annotation { "Feature Type Name" : "Feature", "Feature Type Description" : "" }
export const myFeature = defineFeature(function(context is Context, id is Id, definition is map)
    precondition{}
    {
        {
            var Q0;
            Q0=qCreatedBy(makeId("Front.planeOp"),FACE);
            var sketch = newSketch(context, id + "F0", { "sketchPlane" : qUnion([Q0])});
            skLineSegment(sketch, "E0.bottom", {"start": v(145.5, 75.5) * mm, "end": v(-145.5, 75.5) * mm});
            skLineSegment(sketch, "E0.top", {"start": v(145.5, -75.5) * mm, "end": v(-145.5, -75.5) * mm});
            skLineSegment(sketch, "E0.left", {"start": v(155.5, 65.5) * mm, "end": v(155.5, -65.5) * mm});
            skLineSegment(sketch, "E0.right", {"start": v(-155.5, 65.5) * mm, "end": v(-155.5, -65.5) * mm});
            skPoint(sketch, "E0.middle", {"position": v(0, 0) * mm});
            skLineSegment(sketch, "E1.bottom", {"start": v(135.5, 60.5) * mm, "end": v(-135.5, 60.5) * mm});
            skLineSegment(sketch, "E1.left", {"start": v(140.5, 55.5) * mm, "end": v(140.5, -30.5) * mm});
            skLineSegment(sketch, "E1.right", {"start": v(-140.5, 55.5) * mm, "end": v(-140.5, -35.5) * mm});
            skLineSegment(sketch, "E2", {"start": v(-135.5, -40.5) * mm, "end": v(130.5, -40.5) * mm});
            skPoint(sketch, "E3.orphan", {"position": v(140.5, -60.5) * mm});
            skPoint(sketch, "E4.orphan", {"position": v(-140.5, -60.5) * mm});
            skPoint(sketch, "E5.visualSharp", {"position": v(-155.5, 75.5) * mm});
            skArc(sketch, "E5.filletArc", {"start": v(-145.5, 75.5) * mm, "mid": v(-152.57, 72.57) * mm, "end": v(-155.5, 65.5) * mm});
            skPoint(sketch, "E6.visualSharp", {"position": v(-155.5, -75.5) * mm});
            skArc(sketch, "E6.filletArc", {"start": v(-155.5, -65.5) * mm, "mid": v(-152.57, -72.57) * mm, "end": v(-145.5, -75.5) * mm});
            skPoint(sketch, "E7.visualSharp", {"position": v(155.5, 75.5) * mm});
            skArc(sketch, "E7.filletArc", {"start": v(155.5, 65.5) * mm, "mid": v(152.57, 72.57) * mm, "end": v(145.5, 75.5) * mm});
            skPoint(sketch, "E8.visualSharp", {"position": v(155.5, -75.5) * mm});
            skArc(sketch, "E8.filletArc", {"start": v(145.5, -75.5) * mm, "mid": v(152.57, -72.57) * mm, "end": v(155.5, -65.5) * mm});
            skPoint(sketch, "E9.visualSharp", {"position": v(-140.5, 60.5) * mm});
            skArc(sketch, "E9.filletArc", {"start": v(-135.5, 60.5) * mm, "mid": v(-139.04, 59.04) * mm, "end": v(-140.5, 55.5) * mm});
            skPoint(sketch, "E10.visualSharp", {"position": v(-140.5, -40.5) * mm});
            skArc(sketch, "E10.filletArc", {"start": v(-140.5, -35.5) * mm, "mid": v(-139.04, -39.04) * mm, "end": v(-135.5, -40.5) * mm});
            skPoint(sketch, "E11.visualSharp", {"position": v(140.5, -40.5) * mm});
            skArc(sketch, "E11.filletArc", {"start": v(130.5, -40.5) * mm, "mid": v(137.57, -37.57) * mm, "end": v(140.5, -30.5) * mm});
            skPoint(sketch, "E12.visualSharp", {"position": v(140.5, 60.5) * mm});
            skArc(sketch, "E12.filletArc", {"start": v(140.5, 55.5) * mm, "mid": v(139.04, 59.04) * mm, "end": v(135.5, 60.5) * mm});
            skSolve(sketch);
        }
        {
            var Q0;
            Q0=qSketchRegion(id+"F0",true);
            extrude(context, id + "F1", {"entities" : qUnion([Q0]), "depth" : 1.6 * mm, "offsetDistance" : 25 * mm});
        }
        {
            var Q0;
            Q0=makeQuery(id+"F1.opExtrude","CAP_FACE",FACE,{"disambiguationData":[OSD([sQuery(id+"F0.wireOp",EDGE,"E0.bottom"),sQuery(id+"F0.wireOp",EDGE,"E0.top"),sQuery(id+"F0.wireOp",EDGE,"E0.left"),sQuery(id+"F0.wireOp",EDGE,"E0.right"),sQuery(id+"F0.wireOp",EDGE,"E1.bottom"),sQuery(id+"F0.wireOp",EDGE,"E1.left"),sQuery(id+"F0.wireOp",EDGE,"E1.right"),sQuery(id+"F0.wireOp",EDGE,"E2"),sQuery(id+"F0.wireOp",EDGE,"E5.filletArc"),sQuery(id+"F0.wireOp",EDGE,"E6.filletArc"),sQuery(id+"F0.wireOp",EDGE,"E7.filletArc"),sQuery(id+"F0.wireOp",EDGE,"E8.filletArc"),sQuery(id+"F0.wireOp",EDGE,"E9.filletArc"),sQuery(id+"F0.wireOp",EDGE,"E10.filletArc"),sQuery(id+"F0.wireOp",EDGE,"E11.filletArc"),sQuery(id+"F0.wireOp",EDGE,"E12.filletArc")])],"isStart":false});
            var sketch = newSketch(context, id + "F2", { "sketchPlane" : qUnion([Q0])});
            skLineSegment(sketch, "E13.bottom", {"start": v(-101, 60.5) * mm, "end": v(-76, 60.5) * mm});
            skLineSegment(sketch, "E13.top", {"start": v(-101, 44.5) * mm, "end": v(-76, 44.5) * mm});
            skLineSegment(sketch, "E13.left", {"start": v(-101, 60.5) * mm, "end": v(-101, 44.5) * mm});
            skLineSegment(sketch, "E13.right", {"start": v(-76, 60.5) * mm, "end": v(-76, 44.5) * mm});
            skLineSegment(sketch, "E14.bottom", {"start": v(76, 60.5) * mm, "end": v(101, 60.5) * mm});
            skLineSegment(sketch, "E14.top", {"start": v(76, 44.5) * mm, "end": v(101, 44.5) * mm});
            skLineSegment(sketch, "E14.left", {"start": v(76, 60.5) * mm, "end": v(76, 44.5) * mm});
            skLineSegment(sketch, "E14.right", {"start": v(101, 60.5) * mm, "end": v(101, 44.5) * mm});
            skLineSegment(sketch, "E15", {"start": v(-88.5, 44.5) * mm, "end": v(-88.5, 60.5) * mm, "construction": true});
            skLineSegment(sketch, "E16", {"start": v(-101, 44.5) * mm, "end": v(-140.5, 44.5) * mm, "construction": true});
            skLineSegment(sketch, "E17", {"start": v(101, 44.5) * mm, "end": v(140.5, 44.5) * mm, "construction": true});
            skSolve(sketch);
        }
        {
            var Q0;
            Q0=qSketchRegion(id+"F2",true);
            var Q1;
            Q1=makeQuery(id+"F1.opExtrude","CAP_FACE",FACE,{"disambiguationData":[OSD([sQuery(id+"F0.wireOp",EDGE,"E0.bottom"),sQuery(id+"F0.wireOp",EDGE,"E0.top"),sQuery(id+"F0.wireOp",EDGE,"E0.left"),sQuery(id+"F0.wireOp",EDGE,"E0.right"),sQuery(id+"F0.wireOp",EDGE,"E1.bottom"),sQuery(id+"F0.wireOp",EDGE,"E1.left"),sQuery(id+"F0.wireOp",EDGE,"E1.right"),sQuery(id+"F0.wireOp",EDGE,"E2"),sQuery(id+"F0.wireOp",EDGE,"E5.filletArc"),sQuery(id+"F0.wireOp",EDGE,"E6.filletArc"),sQuery(id+"F0.wireOp",EDGE,"E7.filletArc"),sQuery(id+"F0.wireOp",EDGE,"E8.filletArc"),sQuery(id+"F0.wireOp",EDGE,"E9.filletArc"),sQuery(id+"F0.wireOp",EDGE,"E10.filletArc"),sQuery(id+"F0.wireOp",EDGE,"E11.filletArc"),sQuery(id+"F0.wireOp",EDGE,"E12.filletArc")])],"isStart":true});
            extrude(context, id + "F3", {"entities" : qUnion([Q0]), "operationType" : NewBodyOperationType.ADD, "endBound" : BoundingType.UP_TO_SURFACE, "oppositeDirection" : true, "endBoundEntityFace" : qUnion([Q1]), "depth" : 25 * mm});
        }
        {
            var Q0;
            Q0=makeQuery(id+"F3.boolean.opBoolean","MERGE",FACE,{"derivedFrom":[makeQuery(id+"F1.opExtrude","CAP_FACE",FACE,{"disambiguationData":[OSD([sQuery(id+"F0.wireOp",EDGE,"E0.bottom"),sQuery(id+"F0.wireOp",EDGE,"E0.top"),sQuery(id+"F0.wireOp",EDGE,"E0.left"),sQuery(id+"F0.wireOp",EDGE,"E0.right"),sQuery(id+"F0.wireOp",EDGE,"E1.bottom"),sQuery(id+"F0.wireOp",EDGE,"E1.left"),sQuery(id+"F0.wireOp",EDGE,"E1.right"),sQuery(id+"F0.wireOp",EDGE,"E2"),sQuery(id+"F0.wireOp",EDGE,"E5.filletArc"),sQuery(id+"F0.wireOp",EDGE,"E6.filletArc"),sQuery(id+"F0.wireOp",EDGE,"E7.filletArc"),sQuery(id+"F0.wireOp",EDGE,"E8.filletArc"),sQuery(id+"F0.wireOp",EDGE,"E9.filletArc"),sQuery(id+"F0.wireOp",EDGE,"E10.filletArc"),sQuery(id+"F0.wireOp",EDGE,"E11.filletArc"),sQuery(id+"F0.wireOp",EDGE,"E12.filletArc")])],"isStart":false}),makeQuery(id+"F3.opExtrude","CAP_FACE",FACE,{"disambiguationData":[OSD([sQuery(id+"F2.wireOp",EDGE,"E13.bottom"),sQuery(id+"F2.wireOp",EDGE,"E13.top"),sQuery(id+"F2.wireOp",EDGE,"E13.left"),sQuery(id+"F2.wireOp",EDGE,"E13.right")])],"isStart":true}),makeQuery(id+"F3.opExtrude","CAP_FACE",FACE,{"disambiguationData":[OSD([sQuery(id+"F2.wireOp",EDGE,"E14.bottom"),sQuery(id+"F2.wireOp",EDGE,"E14.top"),sQuery(id+"F2.wireOp",EDGE,"E14.left"),sQuery(id+"F2.wireOp",EDGE,"E14.right")])],"isStart":true})]});
            var sketch = newSketch(context, id + "F4", { "sketchPlane" : qUnion([Q0])});
            skLineSegment(sketch, "E18", {"start": v(101, 60.5) * mm, "end": v(101, 64.5) * mm});
            skLineSegment(sketch, "E19", {"start": v(101, 64.5) * mm, "end": v(140.5, 64.5) * mm});
            skLineSegment(sketch, "E20", {"start": v(140.5, 55.5) * mm, "end": v(101, 55.5) * mm});
            skLineSegment(sketch, "E21", {"start": v(140.5, 55.5) * mm, "end": v(140.5, 64.5) * mm});
            skLineSegment(sketch, "E22", {"start": v(101, 60.5) * mm, "end": v(101, 55.5) * mm});
            skSolve(sketch);
        }
        {
            var Q0;
            Q0=qSketchRegion(id+"F4",true);
            extrude(context, id + "F5", {"entities" : qUnion([Q0]), "operationType" : NewBodyOperationType.REMOVE, "oppositeDirection" : true, "depth" : 25 * mm});
        }
        {
            var Q0;
            Q0=makeQuery(id+"F3.opExtrude","SWEPT_EDGE",EDGE,{"disambiguationData":[OSD([sQuery(id+"F2.wireOp",EDGE,"E13.top"),sQuery(id+"F2.wireOp",EDGE,"E13.left")])]});
            var Q1;
            Q1=makeQuery(id+"F3.opExtrude","SWEPT_EDGE",EDGE,{"disambiguationData":[OSD([sQuery(id+"F0.wireOp",EDGE,"E1.bottom"),sQuery(id+"F2.wireOp",EDGE,"E13.bottom"),sQuery(id+"F2.wireOp",EDGE,"E13.left")])]});
            var Q2;
            Q2=makeQuery(id+"F3.opExtrude","SWEPT_EDGE",EDGE,{"disambiguationData":[OSD([sQuery(id+"F2.wireOp",EDGE,"E13.top"),sQuery(id+"F2.wireOp",EDGE,"E13.right")])]});
            var Q3;
            Q3=makeQuery(id+"F3.opExtrude","SWEPT_EDGE",EDGE,{"disambiguationData":[OSD([sQuery(id+"F0.wireOp",EDGE,"E1.bottom"),sQuery(id+"F2.wireOp",EDGE,"E13.bottom"),sQuery(id+"F2.wireOp",EDGE,"E13.right")])]});
            var Q4;
            Q4=makeQuery(id+"F3.opExtrude","SWEPT_EDGE",EDGE,{"disambiguationData":[OSD([sQuery(id+"F2.wireOp",EDGE,"E14.top"),sQuery(id+"F2.wireOp",EDGE,"E14.right")])]});
            var Q5;
            Q5=makeQuery(id+"F3.opExtrude","SWEPT_EDGE",EDGE,{"disambiguationData":[OSD([sQuery(id+"F0.wireOp",EDGE,"E1.bottom"),sQuery(id+"F2.wireOp",EDGE,"E14.bottom"),sQuery(id+"F2.wireOp",EDGE,"E14.right")])]});
            var Q6;
            Q6=makeQuery(id+"F3.opExtrude","SWEPT_EDGE",EDGE,{"disambiguationData":[OSD([sQuery(id+"F2.wireOp",EDGE,"E14.top"),sQuery(id+"F2.wireOp",EDGE,"E14.left")])]});
            var Q7;
            Q7=makeQuery(id+"F3.opExtrude","SWEPT_EDGE",EDGE,{"disambiguationData":[OSD([sQuery(id+"F0.wireOp",EDGE,"E1.bottom"),sQuery(id+"F2.wireOp",EDGE,"E14.bottom"),sQuery(id+"F2.wireOp",EDGE,"E14.left")])]});
            var Q8;
            Q8=makeQuery(id+"F5.boolean.opBoolean","COPY",EDGE,{"derivedFrom":makeQuery(id+"F5.opExtrude","SWEPT_EDGE",EDGE,{"disambiguationData":[OSD([sQuery(id+"F4.wireOp",EDGE,"E19"),sQuery(id+"F4.wireOp",EDGE,"E21")])]})});
            fillet(context, id + "F6", {"entities" : qUnion([Q0, Q1, Q2, Q3, Q4, Q5, Q6, Q7, Q8]), "radius" : 5 * mm, "tangentPropagation" : true, "allowEdgeOverflow" : false});
        }
        {
            var Q0;
            Q0=makeQuery(id+"F5.boolean.opBoolean","COPY",EDGE,{"derivedFrom":makeQuery(id+"F5.opExtrude","SWEPT_EDGE",EDGE,{"disambiguationData":[OSD([sQuery(id+"F4.wireOp",EDGE,"7OP9Tv27-VSEW-8zX2-RoHM-HqM2cPaEEPGh"),sQuery(id+"F4.wireOp",EDGE,"E18")])]})});
            var Q1;
            Q1=makeQuery(id+"F5.boolean.opBoolean","COPY",EDGE,{"derivedFrom":makeQuery(id+"F5.opExtrude","SWEPT_EDGE",EDGE,{"disambiguationData":[OSD([sQuery(id+"F4.wireOp",EDGE,"aboeoGEW-dTeu-87r4-9ffM-jYBHCW7SDUxB"),sQuery(id+"F4.wireOp",EDGE,"7OP9Tv27-VSEW-8zX2-RoHM-HqM2cPaEEPGh")])]})});
            fillet(context, id + "F7", {"entities" : qUnion([Q0, Q1]), "radius" : 5 * mm, "tangentPropagation" : true, "allowEdgeOverflow" : false});
        }
        {
            var Q0;
            Q0=makeQuery(id+"F3.boolean.opBoolean","MERGE",FACE,{"derivedFrom":[makeQuery(id+"F1.opExtrude","CAP_FACE",FACE,{"disambiguationData":[OSD([sQuery(id+"F0.wireOp",EDGE,"E0.bottom"),sQuery(id+"F0.wireOp",EDGE,"E0.top"),sQuery(id+"F0.wireOp",EDGE,"E0.left"),sQuery(id+"F0.wireOp",EDGE,"E0.right"),sQuery(id+"F0.wireOp",EDGE,"E1.bottom"),sQuery(id+"F0.wireOp",EDGE,"E1.left"),sQuery(id+"F0.wireOp",EDGE,"E1.right"),sQuery(id+"F0.wireOp",EDGE,"E2"),sQuery(id+"F0.wireOp",EDGE,"E5.filletArc"),sQuery(id+"F0.wireOp",EDGE,"E6.filletArc"),sQuery(id+"F0.wireOp",EDGE,"E7.filletArc"),sQuery(id+"F0.wireOp",EDGE,"E8.filletArc"),sQuery(id+"F0.wireOp",EDGE,"E9.filletArc"),sQuery(id+"F0.wireOp",EDGE,"E10.filletArc"),sQuery(id+"F0.wireOp",EDGE,"E11.filletArc"),sQuery(id+"F0.wireOp",EDGE,"E12.filletArc")])],"isStart":false}),makeQuery(id+"F3.opExtrude","CAP_FACE",FACE,{"disambiguationData":[OSD([sQuery(id+"F2.wireOp",EDGE,"E13.bottom"),sQuery(id+"F2.wireOp",EDGE,"E13.top"),sQuery(id+"F2.wireOp",EDGE,"E13.left"),sQuery(id+"F2.wireOp",EDGE,"E13.right")])],"isStart":true}),makeQuery(id+"F3.opExtrude","CAP_FACE",FACE,{"disambiguationData":[OSD([sQuery(id+"F2.wireOp",EDGE,"E14.bottom"),sQuery(id+"F2.wireOp",EDGE,"E14.top"),sQuery(id+"F2.wireOp",EDGE,"E14.left"),sQuery(id+"F2.wireOp",EDGE,"E14.right")])],"isStart":true})]});
            var sketch = newSketch(context, id + "F8", { "sketchPlane" : qUnion([Q0])});
            skCircle(sketch, "E23", {"center": v(-88.5, 56.5) * mm, "radius": 5.5 * mm});
            skCircle(sketch, "E24", {"center": v(88.5, 56.5) * mm, "radius": 5.5 * mm});
            skLineSegment(sketch, "E25", {"start": v(-88.5, 44.5) * mm, "end": v(-88.5, 89.98) * mm, "construction": true});
            skLineSegment(sketch, "E26", {"start": v(88.5, 44.5) * mm, "end": v(88.5, 67.92) * mm, "construction": true});
            skSolve(sketch);
        }
        {
            var Q0;
            Q0=qSketchRegion(id+"F8",true);
            extrude(context, id + "F9", {"entities" : qUnion([Q0]), "operationType" : NewBodyOperationType.REMOVE, "oppositeDirection" : true, "depth" : 25 * mm});
        }
        {
            var Q0;
            Q0=makeQuery(id+"F3.boolean.opBoolean","MERGE",FACE,{"derivedFrom":[makeQuery(id+"F1.opExtrude","CAP_FACE",FACE,{"disambiguationData":[OSD([sQuery(id+"F0.wireOp",EDGE,"E0.bottom"),sQuery(id+"F0.wireOp",EDGE,"E0.top"),sQuery(id+"F0.wireOp",EDGE,"E0.left"),sQuery(id+"F0.wireOp",EDGE,"E0.right"),sQuery(id+"F0.wireOp",EDGE,"E1.bottom"),sQuery(id+"F0.wireOp",EDGE,"E1.left"),sQuery(id+"F0.wireOp",EDGE,"E1.right"),sQuery(id+"F0.wireOp",EDGE,"E2"),sQuery(id+"F0.wireOp",EDGE,"E5.filletArc"),sQuery(id+"F0.wireOp",EDGE,"E6.filletArc"),sQuery(id+"F0.wireOp",EDGE,"E7.filletArc"),sQuery(id+"F0.wireOp",EDGE,"E8.filletArc"),sQuery(id+"F0.wireOp",EDGE,"E9.filletArc"),sQuery(id+"F0.wireOp",EDGE,"E10.filletArc"),sQuery(id+"F0.wireOp",EDGE,"E11.filletArc"),sQuery(id+"F0.wireOp",EDGE,"E12.filletArc")])],"isStart":false}),makeQuery(id+"F3.opExtrude","CAP_FACE",FACE,{"disambiguationData":[OSD([sQuery(id+"F2.wireOp",EDGE,"E13.bottom"),sQuery(id+"F2.wireOp",EDGE,"E13.top"),sQuery(id+"F2.wireOp",EDGE,"E13.left"),sQuery(id+"F2.wireOp",EDGE,"E13.right")])],"isStart":true}),makeQuery(id+"F3.opExtrude","CAP_FACE",FACE,{"disambiguationData":[OSD([sQuery(id+"F2.wireOp",EDGE,"E14.bottom"),sQuery(id+"F2.wireOp",EDGE,"E14.top"),sQuery(id+"F2.wireOp",EDGE,"E14.left"),sQuery(id+"F2.wireOp",EDGE,"E14.right")])],"isStart":true})]});
            var sketch = newSketch(context, id + "F10", { "sketchPlane" : qUnion([Q0]), "disableImprinting" : false});
            skText(sketch, "E27", { "text": "1972", "fontName": "OpenSans-BoldItalic.ttf"});
            const initialGuessF10  = {"E27": [-0.02047, 0.0615, 1, 0, 0.013]};
            skSetInitialGuess(sketch, initialGuessF10);
            skSolve(sketch);
        }
        {
            var Q0;
            {var subQ0=sQuery(id+"F0.wireOp",EDGE,"E0.right");var subQ2=sQuery(id+"F2.wireOp",EDGE,"E14.left");var subQ3=sQuery(id+"F2.wireOp",EDGE,"E14.bottom");var subQ4=sQuery(id+"F0.wireOp",EDGE,"E1.bottom");var subQ5=sQuery(id+"F2.wireOp",EDGE,"E14.right");var subQ6=sQuery(id+"F2.wireOp",EDGE,"E14.top");var subQ7=sQuery(id+"F0.wireOp",EDGE,"E8.filletArc");var subQ8=sQuery(id+"F0.wireOp",EDGE,"E5.filletArc");var subQ9=sQuery(id+"F0.wireOp",EDGE,"E7.filletArc");var subQ10=sQuery(id+"F0.wireOp",EDGE,"E2");var subQ11=sQuery(id+"F0.wireOp",EDGE,"E6.filletArc");var subQ12=sQuery(id+"F0.wireOp",EDGE,"E1.right");var subQ13=sQuery(id+"F2.wireOp",EDGE,"E13.right");var subQ14=sQuery(id+"F2.wireOp",EDGE,"E13.top");var subQ15=sQuery(id+"F0.wireOp",EDGE,"E1.left");var subQ16=sQuery(id+"F0.wireOp",EDGE,"E9.filletArc");var subQ17=sQuery(id+"F2.wireOp",EDGE,"E13.bottom");var subQ18=sQuery(id+"F0.wireOp",EDGE,"E0.bottom");var subQ19=sQuery(id+"F0.wireOp",EDGE,"E0.top");var subQ20=sQuery(id+"F0.wireOp",EDGE,"E0.left");var subQ21=sQuery(id+"F0.wireOp",EDGE,"E10.filletArc");var subQ23=sQuery(id+"F2.wireOp",EDGE,"E13.left");var subQ24=sQuery(id+"F0.wireOp",EDGE,"E11.filletArc");Q0=makeQuery(id+"Fvev97LzUEY7aN8_1.boolean.opBoolean","SPLIT",FACE,{"disambiguationData":[TD([makeQuery(id+"F1.opExtrude","SWEPT_FACE",FACE,{"disambiguationData":[OSD([subQ18])]})])],"derivedFrom":makeQuery(id+"F3.boolean.opBoolean","MERGE",FACE,{"derivedFrom":[makeQuery(id+"F1.opExtrude","CAP_FACE",FACE,{"disambiguationData":[OSD([subQ18,subQ19,subQ20,subQ0,subQ4,subQ15,subQ12,subQ10,subQ8,subQ11,subQ9,subQ7,subQ16,subQ21,subQ24,sQuery(id+"F0.wireOp",EDGE,"E12.filletArc")])],"isStart":false}),makeQuery(id+"F3.opExtrude","CAP_FACE",FACE,{"disambiguationData":[OSD([subQ17,subQ14,subQ23,subQ13])],"isStart":true}),makeQuery(id+"F3.opExtrude","CAP_FACE",FACE,{"disambiguationData":[OSD([subQ3,subQ6,subQ2,subQ5])],"isStart":true})]})});}
            var sketch = newSketch(context, id + "F11", { "sketchPlane" : qUnion([Q0]), "disableImprinting" : false});
            skText(sketch, "E28", { "text": "CHEVY NOVA", "fontName": "OpenSans-BoldItalic.ttf"});
            const initialGuessF11  = {"E28": [-0.1515, -0.0715, 1, 0, 0.03651]};
            skSetInitialGuess(sketch, initialGuessF11);
            skSolve(sketch);
        }
        {
            var Q0;
            {var subQ0=sQuery(id+"F0.wireOp",EDGE,"E12.filletArc");var subQ1=sQuery(id+"F0.wireOp",EDGE,"E11.filletArc");var subQ2=sQuery(id+"F0.wireOp",EDGE,"E10.filletArc");var subQ3=sQuery(id+"F0.wireOp",EDGE,"E9.filletArc");var subQ4=sQuery(id+"F0.wireOp",EDGE,"E8.filletArc");var subQ5=sQuery(id+"F0.wireOp",EDGE,"E7.filletArc");var subQ6=sQuery(id+"F0.wireOp",EDGE,"E6.filletArc");var subQ7=sQuery(id+"F0.wireOp",EDGE,"E5.filletArc");var subQ8=sQuery(id+"F0.wireOp",EDGE,"E2");var subQ9=sQuery(id+"F0.wireOp",EDGE,"E1.right");var subQ10=sQuery(id+"F0.wireOp",EDGE,"E1.left");var subQ11=sQuery(id+"F0.wireOp",EDGE,"E1.bottom");var subQ12=sQuery(id+"F0.wireOp",EDGE,"E0.right");var subQ13=sQuery(id+"F0.wireOp",EDGE,"E0.left");var subQ14=sQuery(id+"F0.wireOp",EDGE,"E0.top");var subQ15=sQuery(id+"F0.wireOp",EDGE,"E0.bottom");Q0=makeQuery(id+"F3.boolean.opBoolean","MERGE",FACE,{"derivedFrom":[makeQuery(id+"F1.opExtrude","CAP_FACE",FACE,{"disambiguationData":[OSD([subQ15,subQ14,subQ13,subQ12,subQ11,subQ10,subQ9,subQ8,subQ7,subQ6,subQ5,subQ4,subQ3,subQ2,subQ1,subQ0])],"isStart":true}),makeQuery(id+"F3.opExtrude","CAP_FACE",FACE,{"disambiguationData":[OSD([subQ15,subQ14,subQ13,subQ12,subQ11,subQ10,subQ9,subQ8,subQ7,subQ6,subQ5,subQ4,subQ3,subQ2,subQ1,subQ0]),ownerDisambiguation([makeQuery(id+"F2.imprint","IMPRINT",EDGE,{"derivedFrom":sQuery(id+"F2.wireOp",EDGE,"E13.bottom")})])],"isStart":false}),makeQuery(id+"F3.opExtrude","CAP_FACE",FACE,{"disambiguationData":[OSD([subQ15,subQ14,subQ13,subQ12,subQ11,subQ10,subQ9,subQ8,subQ7,subQ6,subQ5,subQ4,subQ3,subQ2,subQ1,subQ0]),ownerDisambiguation([makeQuery(id+"F2.imprint","IMPRINT",EDGE,{"derivedFrom":sQuery(id+"F2.wireOp",EDGE,"E14.bottom")})])],"isStart":false})]});}
            var sketch = newSketch(context, id + "F12", { "sketchPlane" : qUnion([Q0])});
            skCircle(sketch, "E29.0", {"center": v(-88.5, 56.5) * mm, "radius": 5.5 * mm});
            skCircle(sketch, "E30.0", {"center": v(88.5, 56.5) * mm, "radius": 5.5 * mm});
            skCircle(sketch, "E31.0", {"center": v(-88.5, 56.5) * mm, "radius": 8.5 * mm});
            skCircle(sketch, "E32.0", {"center": v(88.5, 56.5) * mm, "radius": 8.5 * mm});
            skSolve(sketch);
        }
        {
            var Q0;
            Q0=qSketchRegion(id+"F12",true);
            extrude(context, id + "F13", {"entities" : qUnion([Q0]), "operationType" : NewBodyOperationType.ADD, "depth" : 2 * mm});
        }
        {
            var Q0;
            {var subQ0=sQuery(id+"F0.wireOp",EDGE,"E12.filletArc");var subQ1=sQuery(id+"F0.wireOp",EDGE,"E11.filletArc");var subQ2=sQuery(id+"F0.wireOp",EDGE,"E10.filletArc");var subQ3=sQuery(id+"F0.wireOp",EDGE,"E9.filletArc");var subQ4=sQuery(id+"F0.wireOp",EDGE,"E8.filletArc");var subQ5=sQuery(id+"F0.wireOp",EDGE,"E7.filletArc");var subQ6=sQuery(id+"F0.wireOp",EDGE,"E6.filletArc");var subQ7=sQuery(id+"F0.wireOp",EDGE,"E5.filletArc");var subQ8=sQuery(id+"F0.wireOp",EDGE,"E2");var subQ9=sQuery(id+"F0.wireOp",EDGE,"E1.right");var subQ10=sQuery(id+"F0.wireOp",EDGE,"E1.left");var subQ11=sQuery(id+"F0.wireOp",EDGE,"E1.bottom");var subQ12=sQuery(id+"F0.wireOp",EDGE,"E0.right");var subQ13=sQuery(id+"F0.wireOp",EDGE,"E0.left");var subQ14=sQuery(id+"F0.wireOp",EDGE,"E0.top");var subQ15=sQuery(id+"F0.wireOp",EDGE,"E0.bottom");Q0=makeQuery(id+"F3.boolean.opBoolean","MERGE",FACE,{"derivedFrom":[makeQuery(id+"F1.opExtrude","CAP_FACE",FACE,{"disambiguationData":[OSD([subQ15,subQ14,subQ13,subQ12,subQ11,subQ10,subQ9,subQ8,subQ7,subQ6,subQ5,subQ4,subQ3,subQ2,subQ1,subQ0])],"isStart":true}),makeQuery(id+"F3.opExtrude","CAP_FACE",FACE,{"disambiguationData":[OSD([subQ15,subQ14,subQ13,subQ12,subQ11,subQ10,subQ9,subQ8,subQ7,subQ6,subQ5,subQ4,subQ3,subQ2,subQ1,subQ0]),ownerDisambiguation([makeQuery(id+"F2.imprint","IMPRINT",EDGE,{"derivedFrom":sQuery(id+"F2.wireOp",EDGE,"E13.bottom")})])],"isStart":false}),makeQuery(id+"F3.opExtrude","CAP_FACE",FACE,{"disambiguationData":[OSD([subQ15,subQ14,subQ13,subQ12,subQ11,subQ10,subQ9,subQ8,subQ7,subQ6,subQ5,subQ4,subQ3,subQ2,subQ1,subQ0]),ownerDisambiguation([makeQuery(id+"F2.imprint","IMPRINT",EDGE,{"derivedFrom":sQuery(id+"F2.wireOp",EDGE,"E14.bottom")})])],"isStart":false})]});}
            var sketch = newSketch(context, id + "F14", { "sketchPlane" : qUnion([Q0])});
            skLineSegment(sketch, "E33.0", {"start": v(-155.5, 65.5) * mm, "end": v(-155.5, -65.5) * mm});
            skLineSegment(sketch, "E34.0", {"start": v(-145.5, 75.5) * mm, "end": v(145.5, 75.5) * mm});
            skLineSegment(sketch, "E35.0", {"start": v(155.5, 65.5) * mm, "end": v(155.5, -65.5) * mm});
            skArc(sketch, "E36.0", {"start": v(145.5, 75.5) * mm, "mid": v(152.57, 72.57) * mm, "end": v(155.5, 65.5) * mm});
            skLineSegment(sketch, "E37.0", {"start": v(-153.5, 65.5) * mm, "end": v(-153.5, -65.5) * mm});
            skLineSegment(sketch, "E37.1", {"start": v(153.5, 65.5) * mm, "end": v(153.5, -65.5) * mm});
            skArc(sketch, "E37.2", {"start": v(145.5, 73.5) * mm, "mid": v(151.16, 71.16) * mm, "end": v(153.5, 65.5) * mm});
            skLineSegment(sketch, "E37.3", {"start": v(-145.5, 73.5) * mm, "end": v(145.5, 73.5) * mm});
            skArc(sketch, "E37.4", {"start": v(-153.5, 65.5) * mm, "mid": v(-151.16, 71.16) * mm, "end": v(-145.5, 73.5) * mm});
            skLineSegment(sketch, "E38", {"start": v(-155.5, -65.5) * mm, "end": v(-153.5, -65.5) * mm});
            skLineSegment(sketch, "E39", {"start": v(153.5, -65.5) * mm, "end": v(155.5, -65.5) * mm});
            skSolve(sketch);
        }
        {
            var Q0;
            Q0=makeQuery(id+"F14.imprint","IMPRINT",FACE,{"disambiguationData":[TD([[makeQuery(id+"F14.imprint","IMPRINT",EDGE,{"derivedFrom":sQuery(id+"F14.wireOp",EDGE,"E33.0")}),1.0]])]});
            extrude(context, id + "F15", {"entities" : qUnion([Q0]), "operationType" : NewBodyOperationType.ADD, "depth" : 4.2 * mm});
        }
        {
            var Q0;
            Q0=makeQuery(id+"F15.opExtrude","CAP_FACE",FACE,{"disambiguationData":[OSD([sQuery(id+"F0.wireOp",EDGE,"E7.filletArc"),sQuery(id+"F14.wireOp",EDGE,"E33.0"),sQuery(id+"F14.wireOp",EDGE,"E34.0"),sQuery(id+"F14.wireOp",EDGE,"E35.0"),sQuery(id+"F14.wireOp",EDGE,"E36.0"),sQuery(id+"F14.wireOp",EDGE,"E37.0"),sQuery(id+"F14.wireOp",EDGE,"E37.1"),sQuery(id+"F14.wireOp",EDGE,"E37.2"),sQuery(id+"F14.wireOp",EDGE,"E37.3"),sQuery(id+"F14.wireOp",EDGE,"E37.4"),sQuery(id+"F14.wireOp",EDGE,"E38"),sQuery(id+"F14.wireOp",EDGE,"E39")])],"isStart":false});
            var sketch = newSketch(context, id + "F16", { "sketchPlane" : qUnion([Q0])});
            skLineSegment(sketch, "E40.top", {"start": v(-153.5, -31) * mm, "end": v(-146.5, -31) * mm});
            skLineSegment(sketch, "E40.left", {"start": v(-153.5, 31) * mm, "end": v(-153.5, -31) * mm});
            skLineSegment(sketch, "E40.right", {"start": v(-146.5, 22.66) * mm, "end": v(-146.5, -31) * mm});
            skLineSegment(sketch, "E41", {"start": v(-146.5, 0) * mm, "end": v(-99.43, 0) * mm, "construction": true});
            skLineSegment(sketch, "E42", {"start": v(0, 0) * mm, "end": v(0, 29.16) * mm, "construction": true});
            skLineSegment(sketch, "E43.MirrorCS", {"start": v(153.5, -31) * mm, "end": v(146.5, -31) * mm});
            skLineSegment(sketch, "E44.MirrorCS", {"start": v(153.5, 31) * mm, "end": v(153.5, -31) * mm});
            skLineSegment(sketch, "E45.MirrorCS", {"start": v(146.5, 22.66) * mm, "end": v(146.5, -31) * mm});
            skLineSegment(sketch, "E46", {"start": v(153.5, 31) * mm, "end": v(146.5, 22.66) * mm});
            skPoint(sketch, "E47.MirrorCS.end.orphan", {"position": v(146.5, 31) * mm});
            skPoint(sketch, "E47.MirrorCS.start.orphan", {"position": v(153.5, 31) * mm});
            skLineSegment(sketch, "E48", {"start": v(-153.5, 31) * mm, "end": v(-146.5, 22.66) * mm});
            skPoint(sketch, "E40.bottom.end.orphan", {"position": v(-146.5, 31) * mm});
            skSolve(sketch);
        }
        {
            var Q0;
            Q0=qSketchRegion(id+"F16",true);
            extrude(context, id + "F17", {"entities" : qUnion([Q0]), "operationType" : NewBodyOperationType.ADD, "oppositeDirection" : true, "depth" : 1.6 * mm});
        }
        {
            var Q0;
            Q0=qCreatedBy(makeId("Front.planeOp"),FACE);
            var sketch = newSketch(context, id + "F18", { "sketchPlane" : qUnion([Q0])});
            skLineSegment(sketch, "E49.bottom", {"start": v(-67.55, 81.53) * mm, "end": v(167.55, 81.53) * mm});
            skLineSegment(sketch, "E49.top", {"start": v(-67.55, -113.6) * mm, "end": v(167.55, -113.6) * mm});
            skLineSegment(sketch, "E49.left", {"start": v(167.55, 81.53) * mm, "end": v(167.55, -113.6) * mm});
            skLineSegment(sketch, "E49.right", {"start": v(-67.55, 81.53) * mm, "end": v(-67.55, -113.6) * mm});
            skSolve(sketch);
        }
        {
            var Q0;
            Q0=makeQuery(id+"F10.imprint","IMPRINT",FACE,{"disambiguationData":[TD([[makeQuery(id+"F10.imprint","IMPRINT",EDGE,{"derivedFrom":sQuery(id+"F10.wireOp",EDGE,"E27.sketch_text.stroke-0")}),1.0]])]});
            var sketch = newSketch(context, id + "F19", { "sketchPlane" : qUnion([Q0])});
            skLineSegment(sketch, "E50.bottom", {"start": v(147.1, -43.9) * mm, "end": v(-147.1, -43.9) * mm});
            skLineSegment(sketch, "E50.top", {"start": v(147.1, -73.1) * mm, "end": v(-147.1, -73.1) * mm});
            skLineSegment(sketch, "E50.left", {"start": v(147.1, -43.9) * mm, "end": v(147.1, -73.1) * mm});
            skLineSegment(sketch, "E50.right", {"start": v(-147.1, -43.9) * mm, "end": v(-147.1, -73.1) * mm});
            skPoint(sketch, "E50.middle", {"position": v(0, -58.5) * mm});
            skLineSegment(sketch, "E51", {"start": v(0, 0) * mm, "end": v(0, -13.97) * mm, "construction": true});
            skLineSegment(sketch, "E52.bottom", {"start": v(25.1, 74.6) * mm, "end": v(-25.1, 74.6) * mm});
            skLineSegment(sketch, "E52.top", {"start": v(25.1, 61.4) * mm, "end": v(-25.1, 61.4) * mm});
            skLineSegment(sketch, "E52.left", {"start": v(25.1, 74.6) * mm, "end": v(25.1, 61.4) * mm});
            skLineSegment(sketch, "E52.right", {"start": v(-25.1, 74.6) * mm, "end": v(-25.1, 61.4) * mm});
            skPoint(sketch, "E52.middle", {"position": v(0, 68) * mm});
            skSolve(sketch);
        }
        {
            var Q0;
            Q0 = qSketchRegion(id + "F19", true);
            extrude(context, id + "F20", {"entities" : qUnion([Q0]), "operationType" : NewBodyOperationType.REMOVE, "oppositeDirection" : true, "depth" : .4 * mm, "offsetDistance" : 25 * mm});
        }
    });